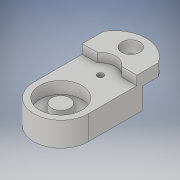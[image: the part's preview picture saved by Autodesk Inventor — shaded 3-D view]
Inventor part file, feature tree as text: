
AUTODESK INVENTOR PART (.ipt)
format: ipt  version: 2018 (Build 220112000, 112)  size: 163,840 bytes
history: native  units: in
note: dims shown in document units (in); Inventor stores cm internally (conversion verified against a paired STEP export)
features: extrude x8, sketch x8
ambient origin geometry x8: Origin, YZ Plane, XZ Plane, XY Plane, X Axis, Y Axis, Z Axis, Center Point
bodies: Solid1 (feature_tree)
feature tree (16):
  extrude  "Extrusion1"  Depth=0.0787in
  extrude  "Extrusion2"  Depth=0.315in
  extrude  "Extrusion3"  Depth=0.1575in TaperAngle=0.0deg
  extrude  "Extrusion4"  Depth=0.7087in
  extrude  "Extrusion5"  Depth=0.1181in
  extrude  "Extrusion6"  Depth=0.2756in TaperAngle=0.0deg
  extrude  "Extrusion7"  Depth=0.3937in
  extrude  "Extrusion9"  [1 undecoded]
  sketch  "Sketch1"  dims[d6=0.0787in d8=0.0787in]
  sketch  "Sketch2"  dims[d9=0.315in d10=0.0in d11=0.2362in]
  sketch  "Sketch3"  dims[d12=0.5512in d13=0.1575in d14=0.0in]
  sketch  "Sketch4"  dims[d15=0.0591in d16=0.0in d17=0.7087in]
  sketch  "Sketch6"  dims[d21=0.1181in d22=0.0in d23=0.4724in]
  sketch  "Sketch7"  dims[d24=0.2756in d25=0.0in d26=0.2756in d27=0.0in]
  sketch  "Sketch8"  dims[d28=0.2756in d29=0.0in d34=0.3937in]
  sketch  "Sketch11"  dims[d35=0.1181in d36=0.0in]
note: 1 required parameter value undecoded (feature->parameter linkage not recoverable at this tier; creation-order binding heuristic only, values carry confidence <= 0.55)
